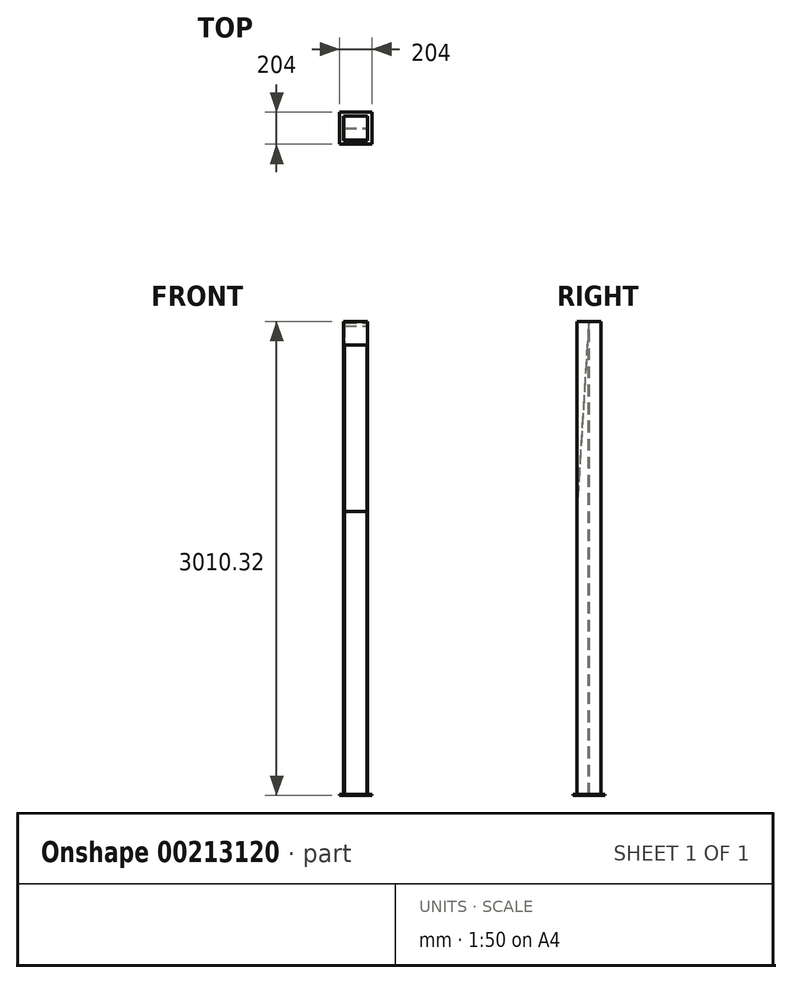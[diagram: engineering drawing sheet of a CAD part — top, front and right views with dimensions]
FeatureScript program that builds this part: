
annotation { "Feature Type Name" : "Feature", "Feature Type Description" : "" }
export const myFeature = defineFeature(function(context is Context, id is Id, definition is map)
    precondition{}
    {
        {
            var Q0;
            Q0=qCreatedBy(makeId("Top.planeOp"),FACE);
            var sketch = newSketch(context, id + "F0", { "sketchPlane" : qUnion([Q0])});
            skLineSegment(sketch, "E0.bottom", {"start": v(-76.2, -76.2) * mm, "end": v(-71.44, -76.2) * mm});
            skLineSegment(sketch, "E0.top", {"start": v(-76.2, 76.2) * mm, "end": v(-71.44, 76.2) * mm});
            skPoint(sketch, "E0.middle", {"position": v(0, 0) * mm});
            skLineSegment(sketch, "E1", {"start": v(-76.2, 76.2) * mm, "end": v(-76.2, -76.2) * mm});
            skLineSegment(sketch, "E2", {"start": v(-71.44, 76.2) * mm, "end": v(-71.44, 2.38) * mm});
            skLineSegment(sketch, "E3", {"start": v(76.2, 76.2) * mm, "end": v(76.2, -76.2) * mm});
            skLineSegment(sketch, "E4", {"start": v(71.44, 76.2) * mm, "end": v(71.44, 2.38) * mm});
            skLineSegment(sketch, "E5.trimOffspring", {"start": v(71.44, 76.2) * mm, "end": v(76.2, 76.2) * mm});
            skLineSegment(sketch, "E6.trimOffspring", {"start": v(71.44, -76.2) * mm, "end": v(76.2, -76.2) * mm});
            skLineSegment(sketch, "E7.0", {"start": v(-71.44, -2.38) * mm, "end": v(71.44, -2.38) * mm});
            skLineSegment(sketch, "E8.0", {"start": v(-71.44, 2.38) * mm, "end": v(71.44, 2.38) * mm});
            skLineSegment(sketch, "E9.trimOffspring", {"start": v(-71.44, -2.38) * mm, "end": v(-71.44, -76.2) * mm});
            skPoint(sketch, "E10.orphan", {"position": v(-71.44, 0) * mm});
            skPoint(sketch, "E11.end.orphan", {"position": v(71.44, 0) * mm});
            skLineSegment(sketch, "E12.trimOffspring", {"start": v(71.44, -2.38) * mm, "end": v(71.44, -76.2) * mm});
            skSolve(sketch);
        }
        {
            var Q0;
            Q0 = qSketchRegion(id + "F0", true);
            extrude(context, id + "F1", {"entities" : qUnion([Q0]), "oppositeDirection" : true, "depth" : 3000 * mm});
        }
        {
            var Q0;
            Q0=makeQuery(id+"F1.opExtrude","CAP_FACE",FACE,{"disambiguationData":[OSD([sQuery(id+"F0.wireOp",EDGE,"E0.bottom"),sQuery(id+"F0.wireOp",EDGE,"E0.top"),sQuery(id+"F0.wireOp",EDGE,"E0.left"),sQuery(id+"F0.wireOp",EDGE,"E0.right"),sQuery(id+"F0.wireOp",EDGE,"7a6f2c26-1c94-48de-b3ff-05aa15f8282d.0"),sQuery(id+"F0.wireOp",EDGE,"bf20579e-0ff9-4312-8226-057ec2ad24a0.0"),sQuery(id+"F0.wireOp",EDGE,"53fb2d3c-9874-4836-9c0b-58f450f03ea0.0"),sQuery(id+"F0.wireOp",EDGE,"893a7bcd-cfe5-4227-b07f-b4167a1dcdd1.0"),sQuery(id+"F0.wireOp",EDGE,"a6ffb2dd-69a9-4642-a933-3686e417fbb3.trimOffspring"),sQuery(id+"F0.wireOp",EDGE,"427ace22-e381-4167-ab2c-954d83dae6c8.trimOffspring"),sQuery(id+"F0.wireOp",EDGE,"ff942871-ae62-4c67-9aaa-94336091cfaf.trimOffspring"),sQuery(id+"F0.wireOp",EDGE,"886b6b8d-e2b2-4d8e-b841-3db4b76343a9.trimOffspring")])],"isStart":true});
            var sketch = newSketch(context, id + "F2", { "sketchPlane" : qUnion([Q0])});
            skLineSegment(sketch, "E13.bottom", {"start": v(-76.2, 76.2) * mm, "end": v(76.2, 76.2) * mm});
            skLineSegment(sketch, "E13.top", {"start": v(-76.2, -76.2) * mm, "end": v(76.2, -76.2) * mm});
            skLineSegment(sketch, "E13.left", {"start": v(-76.2, 76.2) * mm, "end": v(-76.2, -76.2) * mm});
            skLineSegment(sketch, "E13.right", {"start": v(76.2, 76.2) * mm, "end": v(76.2, -76.2) * mm});
            skPoint(sketch, "E13.middle", {"position": v(0, 0) * mm});
            skSolve(sketch);
        }
        {
            var Q0;
            Q0 = qSketchRegion(id + "F2", true);
            extrude(context, id + "F3", {"entities" : qUnion([Q0]), "depth" : 4.76 * mm});
        }
        {
            var Q0;
            Q0=makeQuery(id+"F1.opExtrude","SWEPT_FACE",FACE,{"disambiguationData":[OSD([sQuery(id+"F0.wireOp",EDGE,"E5.trimOffspring")])]});
            var sketch = newSketch(context, id + "F4", { "sketchPlane" : qUnion([Q0])});
            skLineSegment(sketch, "E14.bottom", {"start": v(-76.12, 5.56) * mm, "end": v(75.55, 5.56) * mm});
            skLineSegment(sketch, "E14.top", {"start": v(-76.12, -3000.56) * mm, "end": v(75.55, -3000.56) * mm});
            skLineSegment(sketch, "E14.left", {"start": v(-76.12, 5.56) * mm, "end": v(-76.12, -3000.56) * mm});
            skLineSegment(sketch, "E14.right", {"start": v(75.55, 5.56) * mm, "end": v(75.55, -3000.56) * mm});
            skSolve(sketch);
        }
        {
            var Q0;
            Q0 = qSketchRegion(id + "F4", true);
            extrude(context, id + "F5", {"entities" : qUnion([Q0]), "depth" : 3 / 406.4 * mm});
        }
        {
            var Q0;
            Q0=makeQuery(id+"F3.opExtrude","SWEPT_FACE",FACE,{"disambiguationData":[OSD([sQuery(id+"F2.wireOp",EDGE,"E13.top")])]});
            var sketch = newSketch(context, id + "F6", { "sketchPlane" : qUnion([Q0])});
            skLineSegment(sketch, "E15.bottom", {"start": v(-76.2, 4.76) * mm, "end": v(76.2, 4.76) * mm});
            skLineSegment(sketch, "E15.top", {"start": v(-76.2, -145.24) * mm, "end": v(76.2, -145.24) * mm});
            skLineSegment(sketch, "E15.left", {"start": v(-76.2, 4.76) * mm, "end": v(-76.2, -145.24) * mm});
            skLineSegment(sketch, "E15.right", {"start": v(76.2, 4.76) * mm, "end": v(76.2, -145.24) * mm});
            skSolve(sketch);
        }
        {
            var Q0;
            Q0 = qSketchRegion(id + "F6", true);
            extrude(context, id + "F7", {"entities" : qUnion([Q0]), "depth" : 1.21 * mm});
        }
        {
            var Q0;
            Q0=qCreatedBy(makeId("Right.planeOp"),FACE);
            var sketch = newSketch(context, id + "F8", { "sketchPlane" : qUnion([Q0])});
            skLineSegment(sketch, "E16", {"start": v(-76.91, -1200) * mm, "end": v(73.4, -1200) * mm, "construction": true});
            skLineSegment(sketch, "E17.0", {"start": v(-1.9, 4.32) * mm, "end": v(-77.51, -1199.92) * mm});
            skLineSegment(sketch, "E18.0", {"start": v(-0.7, 4.27) * mm, "end": v(-76.3, -1200.08) * mm});
            skPoint(sketch, "E19.start.orphan", {"position": v(0, 0) * mm});
            skLineSegment(sketch, "E20", {"start": v(-77.51, -1199.92) * mm, "end": v(-76.3, -1200.08) * mm});
            skLineSegment(sketch, "E21", {"start": v(-1.9, 4.32) * mm, "end": v(-0.7, 4.27) * mm});
            skSolve(sketch);
        }
        {
            var Q0;
            Q0 = qSketchRegion(id + "F8", true);
            extrude(context, id + "F9", {"entities" : qUnion([Q0]), "operationType" : NewBodyOperationType.ADD, "endBound" : BoundingType.SYMMETRIC, "depth" : 152.4 * mm - 4.74 * mm - 4.74 * mm});
        }
        {
            var Q0;
            {var subQ1=sQuery(id+"F0.wireOp",EDGE,"E1");var subQ4=sQuery(id+"F0.wireOp",EDGE,"E6.trimOffspring");var subQ5=sQuery(id+"F0.wireOp",EDGE,"E0.bottom");Q0=makeQuery(id+"F7.boolean.opBoolean","SPLIT",FACE,{"disambiguationData":[TD([makeQuery(id+"F1.opExtrude","SWEPT_FACE",FACE,{"disambiguationData":[OSD([subQ1])]})])],"derivedFrom":makeQuery(id+"F3.boolean.opBoolean","MERGE",FACE,{"derivedFrom":[makeQuery(id+"F1.opExtrude","SWEPT_FACE",FACE,{"disambiguationData":[OSD([subQ5])]}),makeQuery(id+"F1.opExtrude","SWEPT_FACE",FACE,{"disambiguationData":[OSD([subQ4])]}),makeQuery(id+"F3.opExtrude","SWEPT_FACE",FACE,{"disambiguationData":[OSD([sQuery(id+"F2.wireOp",EDGE,"E13.top")])]})]})});}
            var sketch = newSketch(context, id + "F10", { "sketchPlane" : qUnion([Q0])});
            skLineSegment(sketch, "E22.bottom", {"start": v(-76.2, -3000) * mm, "end": v(76.2, -3000) * mm});
            skLineSegment(sketch, "E22.top", {"start": v(-76.2, -1200) * mm, "end": v(76.2, -1200) * mm});
            skLineSegment(sketch, "E22.left", {"start": v(-76.2, -3000) * mm, "end": v(-76.2, -1200) * mm});
            skLineSegment(sketch, "E22.right", {"start": v(76.2, -3000) * mm, "end": v(76.2, -1200) * mm});
            skSolve(sketch);
        }
        {
            var Q0;
            Q0 = qSketchRegion(id + "F10", true);
            extrude(context, id + "F11", {"entities" : qUnion([Q0]), "depth" : 3 / 406.4 * mm});
        }
        {
            var Q0;
            Q0=makeQuery(id+"F1.opExtrude","CAP_FACE",FACE,{"disambiguationData":[OSD([sQuery(id+"F0.wireOp",EDGE,"E0.bottom"),sQuery(id+"F0.wireOp",EDGE,"E0.top"),sQuery(id+"F0.wireOp",EDGE,"E1"),sQuery(id+"F0.wireOp",EDGE,"E2"),sQuery(id+"F0.wireOp",EDGE,"E3"),sQuery(id+"F0.wireOp",EDGE,"E4"),sQuery(id+"F0.wireOp",EDGE,"E5.trimOffspring"),sQuery(id+"F0.wireOp",EDGE,"E6.trimOffspring"),sQuery(id+"F0.wireOp",EDGE,"E7.0"),sQuery(id+"F0.wireOp",EDGE,"E8.0"),sQuery(id+"F0.wireOp",EDGE,"E9.trimOffspring"),sQuery(id+"F0.wireOp",EDGE,"E12.trimOffspring")])],"isStart":false});
            var sketch = newSketch(context, id + "F12", { "sketchPlane" : qUnion([Q0])});
            skLineSegment(sketch, "E23.bottom", {"start": v(102, 102) * mm, "end": v(-102, 102) * mm});
            skLineSegment(sketch, "E23.top", {"start": v(102, -102) * mm, "end": v(-102, -102) * mm});
            skLineSegment(sketch, "E23.left", {"start": v(102, 102) * mm, "end": v(102, -102) * mm});
            skLineSegment(sketch, "E23.right", {"start": v(-102, 102) * mm, "end": v(-102, -102) * mm});
            skPoint(sketch, "E23.middle", {"position": v(0, 0) * mm});
            skCircle(sketch, "E24", {"center": v(88.5, 88.5) * mm, "radius": 6.35 * mm, "construction": true});
            skCircle(sketch, "E25.MirrorC", {"center": v(88.5, -88.5) * mm, "radius": 6.35 * mm, "construction": true});
            skCircle(sketch, "E26.MirrorC", {"center": v(-88.5, -88.5) * mm, "radius": 6.35 * mm, "construction": true});
            skCircle(sketch, "E27.MirrorC", {"center": v(-88.5, 88.5) * mm, "radius": 6.35 * mm, "construction": true});
            skSolve(sketch);
        }
        {
            var Q0;
            Q0 = qSketchRegion(id + "F12", true);
            extrude(context, id + "F13", {"entities" : qUnion([Q0]), "depth" : 4.76 * mm});
        }
    });
